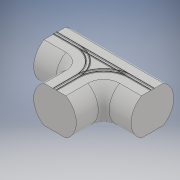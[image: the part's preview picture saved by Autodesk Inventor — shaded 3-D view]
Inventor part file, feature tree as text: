
AUTODESK INVENTOR PART (.ipt)
format: ipt  version: 2017 (Build 210142000, 142)  size: 448,512 bytes
history: native  units: in
note: dims shown in document units (in); Inventor stores cm internally (conversion verified against a paired STEP export)
features: sketch x7, extrude x4, sweep x2, plane x1, mirror x1
ambient origin geometry x8: Origin, YZ Plane, XZ Plane, XY Plane, X Axis, Y Axis, Z Axis, Center Point
bodies: Solid1 (feature_tree)
feature tree (15):
  sketch  "Sketch1"  dims[d0=6.6667in d2=9.7746in d3=4.0in d4=0.0in d5=-4.8873in]
  extrude  "corridor"  [1 undecoded]
  plane  "Work Plane1"
  sketch  "Sketch4"  dims[d6=6.6667in d10=4.0in d11=0.0in d20=0.0in d21=0.0in]
  extrude  "T bottom"  TaperAngle=0.0deg  [1 undecoded]
  sketch  "Sketch8"  dims[d171=4.8873in]
  sketch  "Sketch7"  dims[d22=4.8873in d23=0.0in]
  sweep  "corner curve"
  sketch  "Sketch9"  dims[d187=4.0in d188=0.5833in d189=3.8873in d190=3.8873in d191=1.7083in d192=0.0625in d193=0.0625in d194=1.6458in d195=0.25in d196=0.125in d197=0.0892in d198=0.0884in d199=45.0deg d200=3.3333in d201=0.125in]
  extrude  "flat of T"  TaperAngle=0.0deg  [1 undecoded]
  mirror  "Mirror parts"
  sweep  "corner curve 2"
  extrude  "hole fill in"  [1 undecoded]
  sketch  "Sketch17"  dims[d202=4.0in d203=0.5833in d204=3.8873in d205=3.8873in d206=1.7083in d207=0.0625in d208=0.0625in d209=1.6458in d210=0.25in d211=0.125in d212=0.0892in d213=0.0884in d214=45.0deg d215=3.3333in d216=0.125in d217=0.0in d218=0.0in]
  sketch  "Sketch19"  dims[d219=1.0in d220=0.0in]
note: 4 required parameter values undecoded (feature->parameter linkage not recoverable at this tier; creation-order binding heuristic only, values carry confidence <= 0.55)
